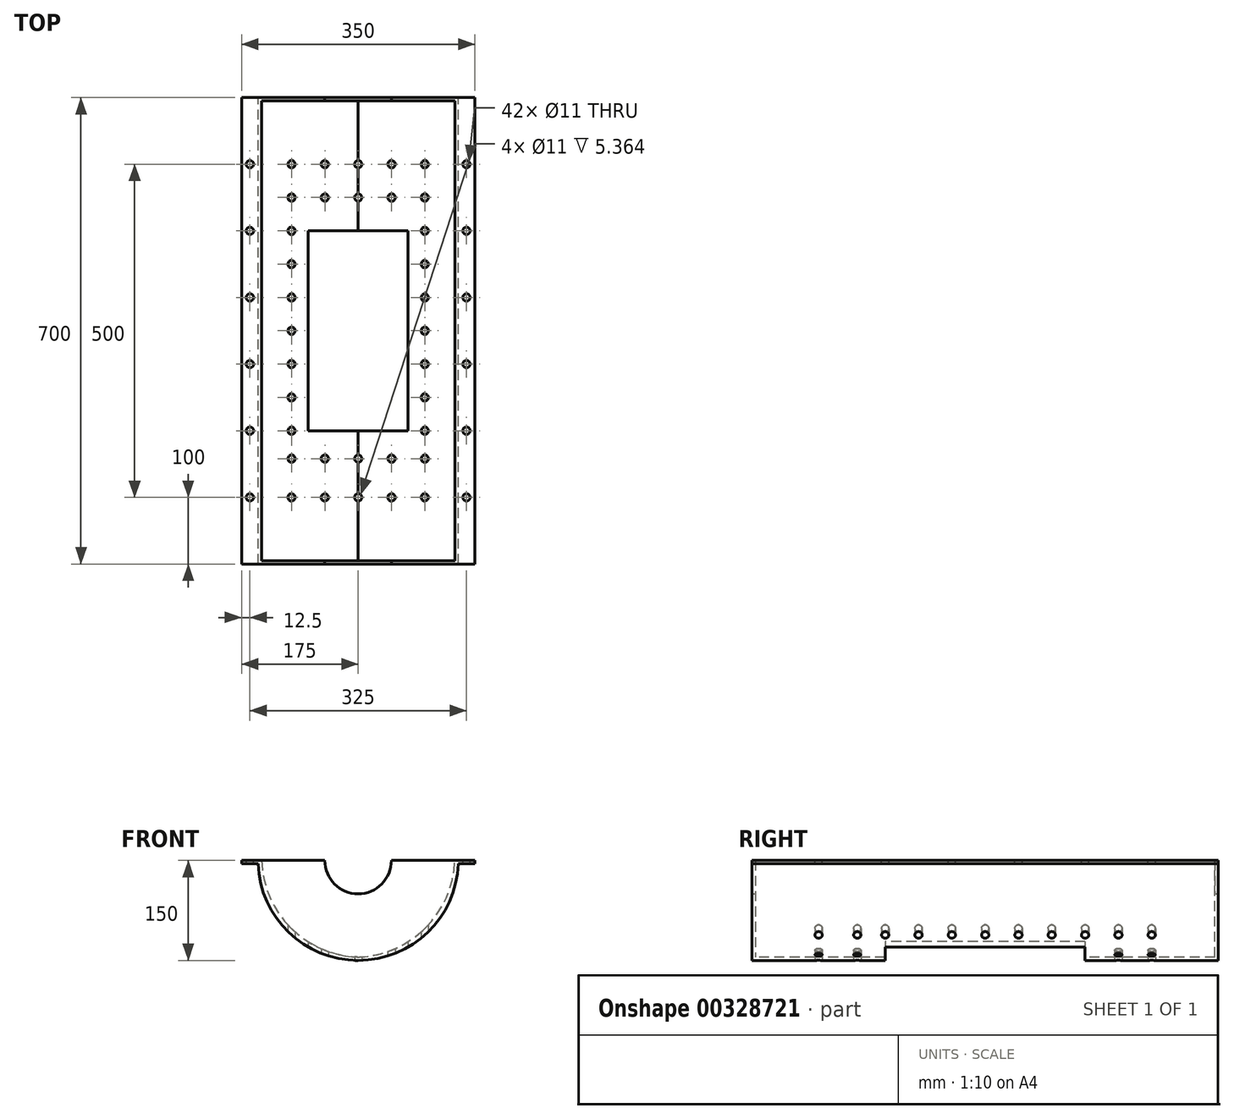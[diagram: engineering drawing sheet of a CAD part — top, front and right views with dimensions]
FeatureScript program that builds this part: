
annotation { "Feature Type Name" : "Feature", "Feature Type Description" : "" }
export const myFeature = defineFeature(function(context is Context, id is Id, definition is map)
    precondition{}
    {
        {
            var Q0;
            Q0=qCreatedBy(makeId("Front.planeOp"),FACE);
            var sketch = newSketch(context, id + "F0", { "sketchPlane" : qUnion([Q0])});
            skLineSegment(sketch, "E0.bottom", {"start": v(150, -75) * mm, "end": v(-150, -75) * mm});
            skLineSegment(sketch, "E0.top", {"start": v(150, 75) * mm, "end": v(50, 75) * mm});
            skLineSegment(sketch, "E0.left", {"start": v(150, -75) * mm, "end": v(150, 70) * mm});
            skLineSegment(sketch, "E0.right", {"start": v(-150, -75) * mm, "end": v(-150, 70) * mm});
            skPoint(sketch, "E0.middle", {"position": v(0, 0) * mm});
            skLineSegment(sketch, "E1", {"start": v(-150, 75) * mm, "end": v(-175, 75) * mm});
            skLineSegment(sketch, "E2", {"start": v(-175, 75) * mm, "end": v(-175, 70) * mm});
            skLineSegment(sketch, "E3", {"start": v(-175, 70) * mm, "end": v(-150, 70) * mm});
            skLineSegment(sketch, "E4", {"start": v(150, 75) * mm, "end": v(175, 75) * mm});
            skLineSegment(sketch, "E5", {"start": v(175, 75) * mm, "end": v(175, 70) * mm});
            skLineSegment(sketch, "E6", {"start": v(175, 70) * mm, "end": v(150, 70) * mm});
            skLineSegment(sketch, "E7.trimOffspring", {"start": v(-50, 75) * mm, "end": v(-150, 75) * mm});
            skPoint(sketch, "E8.center.orphan", {"position": v(0, 75) * mm});
            skLineSegment(sketch, "E9", {"start": v(-50, 75) * mm, "end": v(50, 75) * mm});
            skSolve(sketch);
        }
        {
            var Q0;
            Q0=makeQuery(id+"F0.imprint","IMPRINT",FACE,{"disambiguationData":[TD([[makeQuery(id+"F0.imprint","IMPRINT",EDGE,{"derivedFrom":sQuery(id+"F0.wireOp",EDGE,"E0.bottom")}),-1.0]])]});
            extrude(context, id + "F1", {"entities" : qUnion([Q0]), "depth" : 700 * mm});
        }
        {
            var Q0;
            Q0=makeQuery(id+"F1.opExtrude","SWEPT_FACE",FACE,{"disambiguationData":[OSD([sQuery(id+"F0.wireOp",EDGE,"E0.top"),sQuery(id+"F0.wireOp",EDGE,"E1"),sQuery(id+"F0.wireOp",EDGE,"E4"),sQuery(id+"F0.wireOp",EDGE,"E7.trimOffspring"),sQuery(id+"F0.wireOp",EDGE,"E9")])]});
            var sketch = newSketch(context, id + "F2", { "sketchPlane" : qUnion([Q0])});
            skLineSegment(sketch, "E10.bottom", {"start": v(145, -695) * mm, "end": v(-145, -695) * mm});
            skLineSegment(sketch, "E10.top", {"start": v(145, -5) * mm, "end": v(-145, -5) * mm});
            skLineSegment(sketch, "E10.left", {"start": v(145, -695) * mm, "end": v(145, -5) * mm});
            skLineSegment(sketch, "E10.right", {"start": v(-145, -695) * mm, "end": v(-145, -5) * mm});
            skPoint(sketch, "E10.middle", {"position": v(0, -350) * mm});
            skPoint(sketch, "E10.middle.positionSnap0", {"position": v(175, -350) * mm});
            skPoint(sketch, "E10.middle.positionSnap1", {"position": v(0, 0) * mm});
            skPoint(sketch, "E10.centerSnap0", {"position": v(175, -350) * mm});
            skPoint(sketch, "E10.centerSnap1", {"position": v(0, 0) * mm});
            skSolve(sketch);
        }
        {
            var Q0;
            Q0=makeQuery(id+"F2.imprint","IMPRINT",FACE,{"disambiguationData":[TD([[makeQuery(id+"F2.imprint","IMPRINT",EDGE,{"derivedFrom":sQuery(id+"F2.wireOp",EDGE,"E10.bottom")}),-1.0]])]});
            extrude(context, id + "F3", {"entities" : qUnion([Q0]), "operationType" : NewBodyOperationType.REMOVE, "oppositeDirection" : true, "depth" : 145 * mm});
        }
        {
            var Q0;
            Q0=makeQuery(id+"F1.opExtrude","SWEPT_FACE",FACE,{"disambiguationData":[OSD([sQuery(id+"F0.wireOp",EDGE,"E0.bottom")])]});
            var sketch = newSketch(context, id + "F4", { "sketchPlane" : qUnion([Q0])});
            skLineSegment(sketch, "E11.bottom", {"start": v(75, 500) * mm, "end": v(-75, 500) * mm});
            skLineSegment(sketch, "E11.top", {"start": v(75, 200) * mm, "end": v(-75, 200) * mm});
            skLineSegment(sketch, "E11.left", {"start": v(75, 500) * mm, "end": v(75, 200) * mm});
            skLineSegment(sketch, "E11.right", {"start": v(-75, 500) * mm, "end": v(-75, 200) * mm});
            skPoint(sketch, "E11.middle", {"position": v(0, 350) * mm});
            skPoint(sketch, "E11.middle.positionSnap0", {"position": v(-150, 350) * mm});
            skPoint(sketch, "E11.centerSnap0", {"position": v(-150, 350) * mm});
            skSolve(sketch);
        }
        {
            var Q0;
            Q0=makeQuery(id+"F4.imprint","IMPRINT",FACE,{"disambiguationData":[TD([[makeQuery(id+"F4.imprint","IMPRINT",EDGE,{"derivedFrom":sQuery(id+"F4.wireOp",EDGE,"E11.bottom")}),1.0]])]});
            extrude(context, id + "F5", {"entities" : qUnion([Q0]), "operationType" : NewBodyOperationType.REMOVE, "oppositeDirection" : true, "depth" : 25 * mm});
        }
        {
            var Q0;
            Q0=makeQuery(id+"F1.opExtrude","SWEPT_FACE",FACE,{"disambiguationData":[OSD([sQuery(id+"F0.wireOp",EDGE,"E0.bottom")])]});
            var sketch = newSketch(context, id + "F6", { "sketchPlane" : qUnion([Q0])});
            skCircle(sketch, "E12", {"center": v(-100, 600) * mm, "radius": 10 * mm});
            skCircle(sketch, "E13", {"center": v(-50, 600) * mm, "radius": 10 * mm});
            skCircle(sketch, "E14", {"center": v(0, 600) * mm, "radius": 10 * mm});
            skCircle(sketch, "E15", {"center": v(50, 600) * mm, "radius": 10 * mm});
            skCircle(sketch, "E16", {"center": v(100, 600) * mm, "radius": 10 * mm});
            skCircle(sketch, "E17", {"center": v(-100, 500) * mm, "radius": 10 * mm});
            skCircle(sketch, "E18", {"center": v(100, 500) * mm, "radius": 10 * mm});
            skCircle(sketch, "E19", {"center": v(-50, 541.91) * mm, "radius": 10 * mm});
            skCircle(sketch, "E20", {"center": v(0, 541.91) * mm, "radius": 10 * mm});
            skCircle(sketch, "E21", {"center": v(50, 541.91) * mm, "radius": 10 * mm});
            skCircle(sketch, "E22", {"center": v(100, 541.91) * mm, "radius": 10 * mm});
            skCircle(sketch, "E23", {"center": v(-100, 541.91) * mm, "radius": 10 * mm});
            skCircle(sketch, "E24", {"center": v(100, 450) * mm, "radius": 10 * mm});
            skCircle(sketch, "E25", {"center": v(100, 400) * mm, "radius": 10 * mm});
            skCircle(sketch, "E26", {"center": v(100, 350) * mm, "radius": 10 * mm});
            skCircle(sketch, "E27", {"center": v(100, 300) * mm, "radius": 10 * mm});
            skPoint(sketch, "E28.center.orphan", {"position": v(100, 250) * mm});
            skCircle(sketch, "E29", {"center": v(100, 250) * mm, "radius": 10 * mm});
            skCircle(sketch, "E30", {"center": v(-100, 450) * mm, "radius": 10 * mm});
            skCircle(sketch, "E31", {"center": v(-100, 400) * mm, "radius": 10 * mm});
            skCircle(sketch, "E32", {"center": v(-100, 350) * mm, "radius": 10 * mm});
            skPoint(sketch, "E32.centerSnap0", {"position": v(-75, 350) * mm});
            skCircle(sketch, "E33", {"center": v(-100, 300) * mm, "radius": 10 * mm});
            skCircle(sketch, "E34", {"center": v(-100, 250) * mm, "radius": 10 * mm});
            skCircle(sketch, "E35", {"center": v(-100, 200) * mm, "radius": 10 * mm});
            skCircle(sketch, "E36", {"center": v(100, 200) * mm, "radius": 10 * mm});
            skCircle(sketch, "E37", {"center": v(-100, 150) * mm, "radius": 10 * mm});
            skCircle(sketch, "E38", {"center": v(-50, 150) * mm, "radius": 10 * mm});
            skCircle(sketch, "E39", {"center": v(0, 150) * mm, "radius": 10 * mm});
            skPoint(sketch, "E39.centerSnap0", {"position": v(0, 200) * mm});
            skCircle(sketch, "E40", {"center": v(50, 150) * mm, "radius": 10 * mm});
            skCircle(sketch, "E41", {"center": v(100, 150) * mm, "radius": 10 * mm});
            skCircle(sketch, "E42", {"center": v(-100, 100) * mm, "radius": 10 * mm});
            skCircle(sketch, "E43", {"center": v(-50, 100) * mm, "radius": 10 * mm});
            skCircle(sketch, "E44", {"center": v(0, 100) * mm, "radius": 10 * mm});
            skCircle(sketch, "E45", {"center": v(50, 100) * mm, "radius": 10 * mm});
            skCircle(sketch, "E46", {"center": v(100, 100) * mm, "radius": 10 * mm});
            skSolve(sketch);
        }
        {
            var Q0;
            Q0=sQuery(id+"F6.wireOp",VERTEX,"E12.center");
            var Q1;
            Q1=sQuery(id+"F6.wireOp",VERTEX,"E13.center");
            var Q2;
            Q2=sQuery(id+"F6.wireOp",VERTEX,"E14.center");
            var Q3;
            Q3=sQuery(id+"F6.wireOp",VERTEX,"E15.center");
            var Q4;
            Q4=sQuery(id+"F6.wireOp",VERTEX,"E16.center");
            var Q5;
            Q5=sQuery(id+"F6.wireOp",VERTEX,"E22.center");
            var Q6;
            Q6=sQuery(id+"F6.wireOp",VERTEX,"E21.center");
            var Q7;
            Q7=sQuery(id+"F6.wireOp",VERTEX,"E20.center");
            var Q8;
            Q8=sQuery(id+"F6.wireOp",VERTEX,"E19.center");
            var Q9;
            Q9=sQuery(id+"F6.wireOp",VERTEX,"E23.center");
            var Q10;
            Q10=sQuery(id+"F6.wireOp",VERTEX,"E17.center");
            var Q11;
            Q11=sQuery(id+"F6.wireOp",VERTEX,"E30.center");
            var Q12;
            Q12=sQuery(id+"F6.wireOp",VERTEX,"E31.center");
            var Q13;
            Q13=sQuery(id+"F6.wireOp",VERTEX,"E32.center");
            var Q14;
            Q14=sQuery(id+"F6.wireOp",VERTEX,"E33.center");
            var Q15;
            Q15=sQuery(id+"F6.wireOp",VERTEX,"E34.center");
            var Q16;
            Q16=sQuery(id+"F6.wireOp",VERTEX,"E35.center");
            var Q17;
            Q17=sQuery(id+"F6.wireOp",VERTEX,"E36.center");
            var Q18;
            Q18=sQuery(id+"F6.wireOp",VERTEX,"E28.center.orphan");
            var Q19;
            Q19=sQuery(id+"F6.wireOp",VERTEX,"E27.center");
            var Q20;
            Q20=sQuery(id+"F6.wireOp",VERTEX,"E26.center");
            var Q21;
            Q21=sQuery(id+"F6.wireOp",VERTEX,"E25.center");
            var Q22;
            Q22=sQuery(id+"F6.wireOp",VERTEX,"E24.center");
            var Q23;
            Q23=sQuery(id+"F6.wireOp",VERTEX,"E18.center");
            var Q24;
            Q24=sQuery(id+"F6.wireOp",VERTEX,"E41.center");
            var Q25;
            Q25=sQuery(id+"F6.wireOp",VERTEX,"E40.center");
            var Q26;
            Q26=sQuery(id+"F6.wireOp",VERTEX,"E39.center");
            var Q27;
            Q27=sQuery(id+"F6.wireOp",VERTEX,"E38.center");
            var Q28;
            Q28=sQuery(id+"F6.wireOp",VERTEX,"E37.center");
            var Q29;
            Q29=sQuery(id+"F6.wireOp",VERTEX,"E42.center");
            var Q30;
            Q30=sQuery(id+"F6.wireOp",VERTEX,"E43.center");
            var Q31;
            Q31=sQuery(id+"F6.wireOp",VERTEX,"E44.center");
            var Q32;
            Q32=sQuery(id+"F6.wireOp",VERTEX,"E45.center");
            var Q33;
            Q33=sQuery(id+"F6.wireOp",VERTEX,"E46.center");
            var Q34;
            Q34=makeQuery(id+"F1.opExtrude","SWEPT_BODY",BODY,{"disambiguationData":[OSD([sQuery(id+"F0.wireOp",EDGE,"E0.bottom"),sQuery(id+"F0.wireOp",EDGE,"E0.top"),sQuery(id+"F0.wireOp",EDGE,"E0.left"),sQuery(id+"F0.wireOp",EDGE,"E0.right"),sQuery(id+"F0.wireOp",EDGE,"E1"),sQuery(id+"F0.wireOp",EDGE,"E2"),sQuery(id+"F0.wireOp",EDGE,"E3"),sQuery(id+"F0.wireOp",EDGE,"E4"),sQuery(id+"F0.wireOp",EDGE,"E5"),sQuery(id+"F0.wireOp",EDGE,"E6"),sQuery(id+"F0.wireOp",EDGE,"E7.trimOffspring"),sQuery(id+"F0.wireOp",EDGE,"E9")])]});
            hole(context, id + "F7", {"style" : HoleStyle.SIMPLE, "endStyle" : HoleEndStyle.THROUGH, "standardTappedOrClearance" : lookupTablePath({ "standard" : "ISO", "fit" : "Normal", "size" : "M10", "type" : "Clearance" }), "standardBlindInLast" : lookupTablePath({ "fit" : "Standard", "standard" : "ISO", "size" : "M10", "type" : "Clearance" }), "holeDiameter" : 11 * mm, "isTappedThrough" : true, "tappedDepth" : 14 * mm, "tapClearance" : 3, "locations" : qUnion([Q0, Q1, Q2, Q3, Q4, Q5, Q6, Q7, Q8, Q9, Q10, Q11, Q12, Q13, Q14, Q15, Q16, Q17, Q18, Q19, Q20, Q21, Q22, Q23, Q24, Q25, Q26, Q27, Q28, Q29, Q30, Q31, Q32, Q33]), "scope" : qUnion([Q34])});
        }
        {
            var Q0;
            Q0=makeQuery(id+"F1.opExtrude","SWEPT_FACE",FACE,{"disambiguationData":[OSD([sQuery(id+"F0.wireOp",EDGE,"E0.top"),sQuery(id+"F0.wireOp",EDGE,"E1"),sQuery(id+"F0.wireOp",EDGE,"E4"),sQuery(id+"F0.wireOp",EDGE,"E7.trimOffspring"),sQuery(id+"F0.wireOp",EDGE,"E9")])]});
            var sketch = newSketch(context, id + "F8", { "sketchPlane" : qUnion([Q0])});
            skCircle(sketch, "E47", {"center": v(162.5, -100) * mm, "radius": 5 * mm});
            skCircle(sketch, "E48", {"center": v(162.5, -200) * mm, "radius": 5 * mm});
            skCircle(sketch, "E49", {"center": v(162.5, -300) * mm, "radius": 5 * mm});
            skCircle(sketch, "E50", {"center": v(162.5, -400) * mm, "radius": 5 * mm});
            skCircle(sketch, "E51", {"center": v(162.5, -500) * mm, "radius": 5 * mm});
            skCircle(sketch, "E52", {"center": v(162.5, -600) * mm, "radius": 5 * mm});
            skSolve(sketch);
        }
        {
            var Q0;
            Q0=sQuery(id+"F8.wireOp",VERTEX,"E47.center");
            var Q1;
            Q1=sQuery(id+"F8.wireOp",VERTEX,"E48.center");
            var Q2;
            Q2=sQuery(id+"F8.wireOp",VERTEX,"E49.center");
            var Q3;
            Q3=sQuery(id+"F8.wireOp",VERTEX,"E50.center");
            var Q4;
            Q4=sQuery(id+"F8.wireOp",VERTEX,"E51.center");
            var Q5;
            Q5=sQuery(id+"F8.wireOp",VERTEX,"E52.center");
            var Q6;
            Q6=makeQuery(id+"F1.opExtrude","SWEPT_BODY",BODY,{"disambiguationData":[OSD([sQuery(id+"F0.wireOp",EDGE,"E0.bottom"),sQuery(id+"F0.wireOp",EDGE,"E0.top"),sQuery(id+"F0.wireOp",EDGE,"E0.left"),sQuery(id+"F0.wireOp",EDGE,"E0.right"),sQuery(id+"F0.wireOp",EDGE,"E1"),sQuery(id+"F0.wireOp",EDGE,"E2"),sQuery(id+"F0.wireOp",EDGE,"E3"),sQuery(id+"F0.wireOp",EDGE,"E4"),sQuery(id+"F0.wireOp",EDGE,"E5"),sQuery(id+"F0.wireOp",EDGE,"E6"),sQuery(id+"F0.wireOp",EDGE,"E7.trimOffspring"),sQuery(id+"F0.wireOp",EDGE,"E9")])]});
            hole(context, id + "F9", {"style" : HoleStyle.SIMPLE, "endStyle" : HoleEndStyle.THROUGH, "standardTappedOrClearance" : lookupTablePath({ "standard" : "ISO", "fit" : "Normal", "size" : "M10", "type" : "Clearance" }), "standardBlindInLast" : lookupTablePath({ "fit" : "Standard", "standard" : "ISO", "size" : "M10", "type" : "Clearance" }), "holeDiameter" : 11 * mm, "isTappedThrough" : true, "tappedDepth" : 14 * mm, "tapClearance" : 3, "locations" : qUnion([Q0, Q1, Q2, Q3, Q4, Q5]), "scope" : qUnion([Q6])});
        }
        {
            var Q0;
            Q0=makeQuery(id+"F1.opExtrude","SWEPT_FACE",FACE,{"disambiguationData":[OSD([sQuery(id+"F0.wireOp",EDGE,"E0.top"),sQuery(id+"F0.wireOp",EDGE,"E1"),sQuery(id+"F0.wireOp",EDGE,"E4"),sQuery(id+"F0.wireOp",EDGE,"E7.trimOffspring"),sQuery(id+"F0.wireOp",EDGE,"E9")])]});
            var sketch = newSketch(context, id + "F10", { "sketchPlane" : qUnion([Q0])});
            skCircle(sketch, "E53", {"center": v(-162.5, -100) * mm, "radius": 5 * mm});
            skCircle(sketch, "E54", {"center": v(-162.5, -200) * mm, "radius": 5 * mm});
            skCircle(sketch, "E55", {"center": v(-162.5, -300) * mm, "radius": 5 * mm});
            skCircle(sketch, "E56", {"center": v(-162.5, -400) * mm, "radius": 5 * mm});
            skCircle(sketch, "E57", {"center": v(-162.5, -500) * mm, "radius": 5 * mm});
            skCircle(sketch, "E58", {"center": v(-162.5, -600) * mm, "radius": 5 * mm});
            skSolve(sketch);
        }
        {
            var Q0;
            Q0=sQuery(id+"F10.wireOp",VERTEX,"E53.center");
            var Q1;
            Q1=sQuery(id+"F10.wireOp",VERTEX,"E54.center");
            var Q2;
            Q2=sQuery(id+"F10.wireOp",VERTEX,"E55.center");
            var Q3;
            Q3=sQuery(id+"F10.wireOp",VERTEX,"E56.center");
            var Q4;
            Q4=sQuery(id+"F10.wireOp",VERTEX,"E57.center");
            var Q5;
            Q5=sQuery(id+"F10.wireOp",VERTEX,"E58.center");
            var Q6;
            Q6=makeQuery(id+"F1.opExtrude","SWEPT_BODY",BODY,{"disambiguationData":[OSD([sQuery(id+"F0.wireOp",EDGE,"E0.bottom"),sQuery(id+"F0.wireOp",EDGE,"E0.top"),sQuery(id+"F0.wireOp",EDGE,"E0.left"),sQuery(id+"F0.wireOp",EDGE,"E0.right"),sQuery(id+"F0.wireOp",EDGE,"E1"),sQuery(id+"F0.wireOp",EDGE,"E2"),sQuery(id+"F0.wireOp",EDGE,"E3"),sQuery(id+"F0.wireOp",EDGE,"E4"),sQuery(id+"F0.wireOp",EDGE,"E5"),sQuery(id+"F0.wireOp",EDGE,"E6"),sQuery(id+"F0.wireOp",EDGE,"E7.trimOffspring"),sQuery(id+"F0.wireOp",EDGE,"E9")])]});
            hole(context, id + "F11", {"style" : HoleStyle.SIMPLE, "endStyle" : HoleEndStyle.THROUGH, "standardTappedOrClearance" : lookupTablePath({ "standard" : "ISO", "fit" : "Normal", "size" : "M10", "type" : "Clearance" }), "standardBlindInLast" : lookupTablePath({ "fit" : "Standard", "standard" : "ISO", "size" : "M10", "type" : "Clearance" }), "holeDiameter" : 11 * mm, "isTappedThrough" : true, "tappedDepth" : 14 * mm, "tapClearance" : 3, "locations" : qUnion([Q0, Q1, Q2, Q3, Q4, Q5]), "scope" : qUnion([Q6])});
        }
        {
            var Q0;
            Q0=makeQuery(id+"F3.boolean.opBoolean","COPY",EDGE,{"derivedFrom":makeQuery(id+"F3.opExtrude","CAP_EDGE",EDGE,{"disambiguationData":[OSD([sQuery(id+"F2.wireOp",EDGE,"E10.right")])],"isStart":false})});
            var Q1;
            Q1=makeQuery(id+"F3.boolean.opBoolean","COPY",EDGE,{"derivedFrom":makeQuery(id+"F3.opExtrude","CAP_EDGE",EDGE,{"disambiguationData":[OSD([sQuery(id+"F2.wireOp",EDGE,"E10.left")])],"isStart":false})});
            fillet(context, id + "F12", {"entities" : qUnion([Q0, Q1]), "radius" : 150 * mm, "tangentPropagation" : true, "allowEdgeOverflow" : false});
        }
        {
            var Q0;
            Q0=makeQuery(id+"F1.opExtrude","SWEPT_EDGE",EDGE,{"disambiguationData":[OSD([sQuery(id+"F0.wireOp",EDGE,"E0.bottom"),sQuery(id+"F0.wireOp",EDGE,"E0.left")])]});
            var Q1;
            Q1=makeQuery(id+"F1.opExtrude","SWEPT_EDGE",EDGE,{"disambiguationData":[OSD([sQuery(id+"F0.wireOp",EDGE,"E0.bottom"),sQuery(id+"F0.wireOp",EDGE,"E0.right")])]});
            fillet(context, id + "F13", {"entities" : qUnion([Q0, Q1]), "radius" : 150 * mm, "tangentPropagation" : true, "allowEdgeOverflow" : false});
        }
        {
            var Q0;
            Q0=makeQuery(id+"F1.opExtrude","CAP_FACE",FACE,{"disambiguationData":[OSD([sQuery(id+"F0.wireOp",EDGE,"E0.bottom"),sQuery(id+"F0.wireOp",EDGE,"E0.top"),sQuery(id+"F0.wireOp",EDGE,"E0.left"),sQuery(id+"F0.wireOp",EDGE,"E0.right"),sQuery(id+"F0.wireOp",EDGE,"E1"),sQuery(id+"F0.wireOp",EDGE,"E2"),sQuery(id+"F0.wireOp",EDGE,"E3"),sQuery(id+"F0.wireOp",EDGE,"E4"),sQuery(id+"F0.wireOp",EDGE,"E5"),sQuery(id+"F0.wireOp",EDGE,"E6"),sQuery(id+"F0.wireOp",EDGE,"E7.trimOffspring"),sQuery(id+"F0.wireOp",EDGE,"E9")])],"isStart":true});
            var sketch = newSketch(context, id + "F14", { "sketchPlane" : qUnion([Q0])});
            skCircle(sketch, "E59", {"center": v(0.08, 75) * mm, "radius": 50 * mm});
            skSolve(sketch);
        }
        {
            var Q0;
            {var subQ0=sQuery(id+"F14.wireOp",EDGE,"E59");var subQ1=makeQuery(id+"F1.opExtrude","CAP_EDGE",EDGE,{"disambiguationData":[OSD([sQuery(id+"F0.wireOp",EDGE,"E0.top"),sQuery(id+"F0.wireOp",EDGE,"E1"),sQuery(id+"F0.wireOp",EDGE,"E4"),sQuery(id+"F0.wireOp",EDGE,"E7.trimOffspring"),sQuery(id+"F0.wireOp",EDGE,"E9")])],"isStart":true});var subQ2=makeQuery(id+"F14.imprint","INTERSECT",VERTEX,{"disambiguationData":[OD(0.0)],"derivedFrom":[subQ1,subQ0]});Q0=makeQuery(id+"F14.imprint","IMPRINT",FACE,{"disambiguationData":[TD([[makeQuery(id+"F14.imprint","IMPRINT",EDGE,{"disambiguationData":[TD([[subQ2,-1.0]])],"derivedFrom":subQ0}),1.0]])]});}
            var Q1;
            {var subQ0=sQuery(id+"F14.wireOp",EDGE,"E59");var subQ1=makeQuery(id+"F1.opExtrude","CAP_EDGE",EDGE,{"disambiguationData":[OSD([sQuery(id+"F0.wireOp",EDGE,"E0.top"),sQuery(id+"F0.wireOp",EDGE,"E1"),sQuery(id+"F0.wireOp",EDGE,"E4"),sQuery(id+"F0.wireOp",EDGE,"E7.trimOffspring"),sQuery(id+"F0.wireOp",EDGE,"E9")])],"isStart":true});var subQ2=makeQuery(id+"F14.imprint","INTERSECT",VERTEX,{"disambiguationData":[OD(0.0)],"derivedFrom":[subQ1,subQ0]});Q1=makeQuery(id+"F14.imprint","IMPRINT",FACE,{"disambiguationData":[TD([[makeQuery(id+"F14.imprint","IMPRINT",EDGE,{"disambiguationData":[TD([[subQ2,1.0]])],"derivedFrom":subQ0}),1.0]])]});}
            extrude(context, id + "F15", {"entities" : qUnion([Q0, Q1]), "operationType" : NewBodyOperationType.REMOVE, "oppositeDirection" : true, "depth" : 700 * mm});
        }
    });
